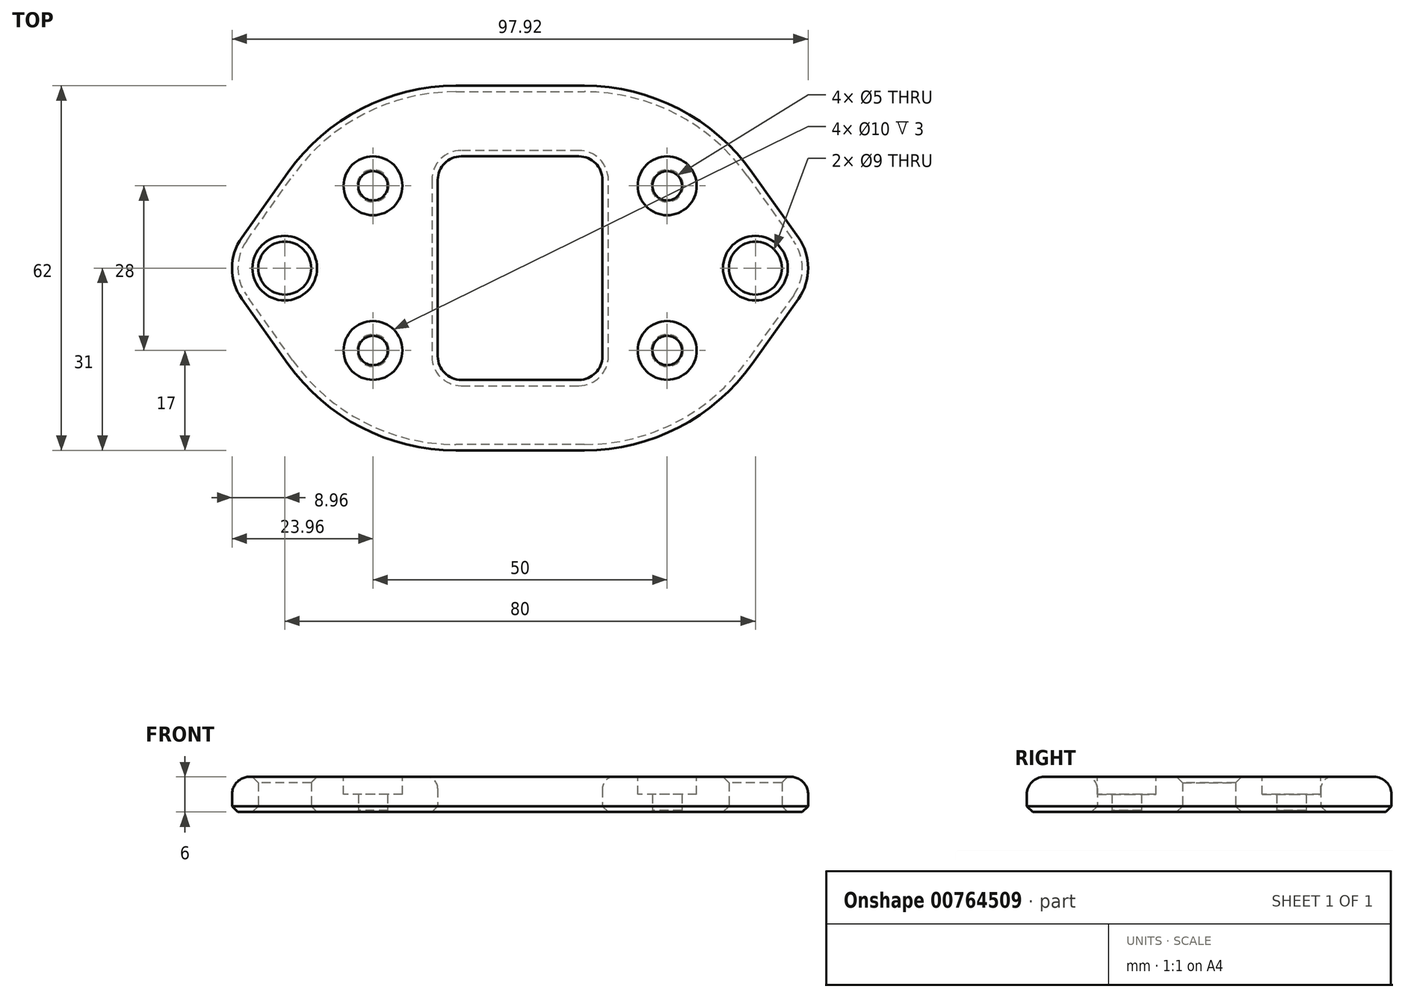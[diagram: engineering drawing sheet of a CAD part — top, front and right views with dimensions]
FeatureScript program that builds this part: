
annotation { "Feature Type Name" : "Feature", "Feature Type Description" : "" }
export const myFeature = defineFeature(function(context is Context, id is Id, definition is map)
    precondition{}
    {
        {
            var Q0;
            Q0=qCreatedBy(makeId("Top.planeOp"),FACE);
            var sketch = newSketch(context, id + "F0", { "sketchPlane" : qUnion([Q0])});
            skLineSegment(sketch, "E0", {"start": v(0, 24.52) * mm, "end": v(0, -20.17) * mm, "construction": true});
            skLineSegment(sketch, "E1", {"start": v(-29.41, 0) * mm, "end": v(36.17, 0) * mm, "construction": true});
            skCircle(sketch, "E2", {"center": v(-25, 14) * mm, "radius": 2.5 * mm});
            skCircle(sketch, "E3", {"center": v(-40, 0) * mm, "radius": 4.5 * mm});
            skLineSegment(sketch, "E4", {"start": v(0, 19) * mm, "end": v(-10, 19) * mm});
            skLineSegment(sketch, "E5", {"start": v(-14, 15) * mm, "end": v(-14, 10) * mm});
            skLineSegment(sketch, "E6", {"start": v(-20.5, 8) * mm, "end": v(-20.5, 8) * mm});
            skPoint(sketch, "E7.orphan", {"position": v(-14, 0) * mm});
            skPoint(sketch, "E8.visualSharp", {"position": v(-14, 19) * mm});
            skArc(sketch, "E8.filletArc", {"start": v(-10, 19) * mm, "mid": v(-12.83, 17.83) * mm, "end": v(-14, 15) * mm});
            skPoint(sketch, "E9.visualSharp", {"position": v(-14, 8) * mm});
            skPoint(sketch, "E10.visualSharp", {"position": v(-22.5, 8) * mm});
            skLineSegment(sketch, "E11.MirrorCS", {"start": v(-20.5, -8) * mm, "end": v(-20.5, -8) * mm});
            skLineSegment(sketch, "E12.MirrorCS", {"start": v(-14, -15) * mm, "end": v(-14, -10) * mm});
            skArc(sketch, "E13.MirrorCS", {"start": v(-10, -19) * mm, "mid": v(-12.83, -17.83) * mm, "end": v(-14, -15) * mm});
            skPoint(sketch, "E14.MirrorP", {"position": v(-14, -8) * mm});
            skPoint(sketch, "E15.MirrorP", {"position": v(-22.5, -8) * mm});
            skPoint(sketch, "E16.MirrorP", {"position": v(-14, -19) * mm});
            skCircle(sketch, "E17.MirrorC", {"center": v(-25, -14) * mm, "radius": 2.5 * mm});
            skLineSegment(sketch, "E18.MirrorCS", {"start": v(0, -19) * mm, "end": v(-10, -19) * mm});
            skLineSegment(sketch, "E19", {"start": v(0, -31) * mm, "end": v(-10.92, -31) * mm});
            skPoint(sketch, "E20", {"position": v(-51, 0) * mm});
            skLineSegment(sketch, "E21", {"start": v(-47.3, -5.2) * mm, "end": v(-39.46, -16.26) * mm});
            skLineSegment(sketch, "E22", {"start": v(0, 31) * mm, "end": v(-10.92, 31) * mm});
            skLineSegment(sketch, "E23", {"start": v(-39.46, 16.26) * mm, "end": v(-47.3, 5.2) * mm});
            skArc(sketch, "E24.filletArc", {"start": v(-47.3, 5.2) * mm, "mid": v(-48.96, 0) * mm, "end": v(-47.3, -5.2) * mm});
            skPoint(sketch, "E25.visualSharp", {"position": v(-29, -31) * mm});
            skArc(sketch, "E25.filletArc", {"start": v(-39.46, -16.26) * mm, "mid": v(-26.98, -27.1) * mm, "end": v(-10.92, -31) * mm});
            skPoint(sketch, "E26.visualSharp", {"position": v(-29, 31) * mm});
            skArc(sketch, "E26.filletArc", {"start": v(-10.92, 31) * mm, "mid": v(-26.98, 27.1) * mm, "end": v(-39.46, 16.26) * mm});
            skLineSegment(sketch, "E27.MirrorCS", {"start": v(20.5, -8) * mm, "end": v(20.5, -8) * mm});
            skLineSegment(sketch, "E28.MirrorCS", {"start": v(20.5, 8) * mm, "end": v(20.5, 8) * mm});
            skArc(sketch, "E29.MirrorCS", {"start": v(47.3, 5.2) * mm, "mid": v(48.96, 0) * mm, "end": v(47.3, -5.2) * mm});
            skLineSegment(sketch, "E30.MirrorCS", {"start": v(14, 15) * mm, "end": v(14, 10) * mm});
            skLineSegment(sketch, "E31.MirrorCS", {"start": v(14, -15) * mm, "end": v(14, -10) * mm});
            skPoint(sketch, "E32.MirrorP", {"position": v(51, 0) * mm});
            skArc(sketch, "E33.MirrorCS", {"start": v(10, -19) * mm, "mid": v(12.83, -17.83) * mm, "end": v(14, -15) * mm});
            skArc(sketch, "E34.MirrorCS", {"start": v(10, 19) * mm, "mid": v(12.83, 17.83) * mm, "end": v(14, 15) * mm});
            skArc(sketch, "E35.MirrorCS", {"start": v(39.46, -16.26) * mm, "mid": v(26.98, -27.1) * mm, "end": v(10.92, -31) * mm});
            skCircle(sketch, "E36.MirrorC", {"center": v(25, -14) * mm, "radius": 2.5 * mm});
            skPoint(sketch, "E37.MirrorP", {"position": v(22.5, -8) * mm});
            skLineSegment(sketch, "E38.MirrorCS", {"start": v(47.3, -5.2) * mm, "end": v(39.46, -16.26) * mm});
            skLineSegment(sketch, "E39.MirrorCS", {"start": v(39.46, 16.26) * mm, "end": v(47.3, 5.2) * mm});
            skArc(sketch, "E40.MirrorCS", {"start": v(10.92, 31) * mm, "mid": v(26.98, 27.1) * mm, "end": v(39.46, 16.26) * mm});
            skPoint(sketch, "E41.MirrorP", {"position": v(22.5, 8) * mm});
            skPoint(sketch, "E42.MirrorP", {"position": v(14, 19) * mm});
            skPoint(sketch, "E43.MirrorP", {"position": v(29, -31) * mm});
            skPoint(sketch, "E44.MirrorP", {"position": v(14, 0) * mm});
            skPoint(sketch, "E45.MirrorP", {"position": v(29, 31) * mm});
            skCircle(sketch, "E46.MirrorC", {"center": v(40, 0) * mm, "radius": 4.5 * mm});
            skPoint(sketch, "E47.MirrorP", {"position": v(14, -8) * mm});
            skCircle(sketch, "E48.MirrorC", {"center": v(25, 14) * mm, "radius": 2.5 * mm});
            skPoint(sketch, "E49.MirrorP", {"position": v(14, 8) * mm});
            skPoint(sketch, "E50.MirrorP", {"position": v(14, -19) * mm});
            skLineSegment(sketch, "E51.MirrorCS", {"start": v(0, 31) * mm, "end": v(10.92, 31) * mm});
            skLineSegment(sketch, "E52.MirrorCS", {"start": v(0, 19) * mm, "end": v(10, 19) * mm});
            skLineSegment(sketch, "E53.MirrorCS", {"start": v(0, -19) * mm, "end": v(10, -19) * mm});
            skLineSegment(sketch, "E54.MirrorCS", {"start": v(0, -31) * mm, "end": v(10.92, -31) * mm});
            skLineSegment(sketch, "E55", {"start": v(-14, 10) * mm, "end": v(-14, -10) * mm});
            skLineSegment(sketch, "E56", {"start": v(14, 10) * mm, "end": v(14, -10) * mm});
            skPoint(sketch, "E57.MirrorCS.end.orphan", {"position": v(22.5, 0) * mm});
            skPoint(sketch, "E57.MirrorCS.start.orphan", {"position": v(22.5, 6) * mm});
            skPoint(sketch, "E58.MirrorCS.start.orphan", {"position": v(22.5, -6) * mm});
            skPoint(sketch, "E59.end.orphan", {"position": v(-22.5, 0) * mm});
            skPoint(sketch, "E59.start.orphan", {"position": v(-22.5, 6) * mm});
            skPoint(sketch, "E60.MirrorCS.start.orphan", {"position": v(-22.5, -6) * mm});
            skSolve(sketch);
        }
        {
            var Q0;
            Q0=qSketchRegion(id+"F0",true);
            extrude(context, id + "F1", {"entities" : qUnion([Q0]), "depth" : 6 * mm, "offsetDistance" : 25 * mm});
        }
        {
            var Q0;
            {var subQ0=sQuery(id+"F0.wireOp",EDGE,"E40.MirrorCS");var subQ1=sQuery(id+"F0.wireOp",EDGE,"E39.MirrorCS");var subQ2=sQuery(id+"F0.wireOp",EDGE,"E57.MirrorCS");var subQ3=sQuery(id+"F0.wireOp",EDGE,"E58.MirrorCS");var subQ4=sQuery(id+"F0.wireOp",EDGE,"E34.MirrorCS");var subQ5=sQuery(id+"F0.wireOp",EDGE,"E26.filletArc");var subQ6=sQuery(id+"F0.wireOp",EDGE,"E24.filletArc");var subQ7=sQuery(id+"F0.wireOp",EDGE,"E23");var subQ8=sQuery(id+"F0.wireOp",EDGE,"E29.MirrorCS");var subQ9=sQuery(id+"F0.wireOp",EDGE,"E52.MirrorCS");var subQ10=sQuery(id+"F0.wireOp",EDGE,"E4");var subQ11=sQuery(id+"F0.wireOp",EDGE,"E28.MirrorCS");var subQ12=sQuery(id+"F0.wireOp",EDGE,"E3");var subQ13=sQuery(id+"F0.wireOp",EDGE,"E5");var subQ14=sQuery(id+"F0.wireOp",EDGE,"E2");var subQ15=sQuery(id+"F0.wireOp",EDGE,"E6");var subQ16=sQuery(id+"F0.wireOp",EDGE,"a55919db-5f6a-430a-85d6-64e5501b8bc05.MirrorCS");var subQ17=sQuery(id+"F0.wireOp",EDGE,"E60.MirrorCS");var subQ18=sQuery(id+"F0.wireOp",EDGE,"E59");var subQ19=sQuery(id+"F0.wireOp",EDGE,"E30.MirrorCS");var subQ20=sQuery(id+"F0.wireOp",EDGE,"E8.filletArc");var subQ21=sQuery(id+"F0.wireOp",EDGE,"a55919db-5f6a-430a-85d6-64e5501b8bc07.MirrorCS");var subQ22=sQuery(id+"F0.wireOp",EDGE,"E9.filletArc");var subQ23=sQuery(id+"F0.wireOp",EDGE,"E51.MirrorCS");var subQ24=sQuery(id+"F0.wireOp",EDGE,"E22");var subQ25=sQuery(id+"F0.wireOp",EDGE,"E10.filletArc");var subQ26=sQuery(id+"F0.wireOp",EDGE,"E46.MirrorC");var subQ27=sQuery(id+"F0.wireOp",EDGE,"E48.MirrorC");Q0=makeQuery(id+"F5VNmm26oAdcOlD_1.boolean.opBoolean","SPLIT",FACE,{"disambiguationData":[TD([makeQuery(id+"F1.opExtrude","SWEPT_FACE",FACE,{"disambiguationData":[OSD([subQ14])]})])],"derivedFrom":makeQuery(id+"F1.opExtrude","CAP_FACE",FACE,{"disambiguationData":[OSD([subQ14,subQ12,subQ10,subQ13,subQ15,subQ18,subQ20,subQ22,subQ25,sQuery(id+"F0.wireOp",EDGE,"27876a6a-8a0b-4b51-943c-244007aa9b000.MirrorCS"),sQuery(id+"F0.wireOp",EDGE,"27876a6a-8a0b-4b51-943c-244007aa9b001.MirrorCS"),sQuery(id+"F0.wireOp",EDGE,"E11.MirrorCS"),sQuery(id+"F0.wireOp",EDGE,"E12.MirrorCS"),sQuery(id+"F0.wireOp",EDGE,"E13.MirrorCS"),sQuery(id+"F0.wireOp",EDGE,"E17.MirrorC"),sQuery(id+"F0.wireOp",EDGE,"E18.MirrorCS"),subQ17,sQuery(id+"F0.wireOp",EDGE,"E19"),sQuery(id+"F0.wireOp",EDGE,"E21"),subQ24,subQ7,subQ6,sQuery(id+"F0.wireOp",EDGE,"E25.filletArc"),subQ5,sQuery(id+"F0.wireOp",EDGE,"E27.MirrorCS"),subQ11,subQ8,sQuery(id+"F0.wireOp",EDGE,"a55919db-5f6a-430a-85d6-64e5501b8bc03.MirrorCS"),sQuery(id+"F0.wireOp",EDGE,"a55919db-5f6a-430a-85d6-64e5501b8bc04.MirrorCS"),subQ16,subQ19,subQ21,sQuery(id+"F0.wireOp",EDGE,"E31.MirrorCS"),sQuery(id+"F0.wireOp",EDGE,"E33.MirrorCS"),subQ4,sQuery(id+"F0.wireOp",EDGE,"E35.MirrorCS"),sQuery(id+"F0.wireOp",EDGE,"E36.MirrorC"),subQ3,sQuery(id+"F0.wireOp",EDGE,"E38.MirrorCS"),subQ1,subQ0,subQ26,subQ27,subQ2,subQ23,subQ9,sQuery(id+"F0.wireOp",EDGE,"E53.MirrorCS"),sQuery(id+"F0.wireOp",EDGE,"E54.MirrorCS")])],"isStart":false})});}
            var sketch = newSketch(context, id + "F2", { "sketchPlane" : qUnion([Q0])});
            skCircle(sketch, "E61", {"center": v(-25, 14) * mm, "radius": 5 * mm});
            skCircle(sketch, "E62", {"center": v(25, 14) * mm, "radius": 5 * mm});
            skCircle(sketch, "E63", {"center": v(25, -14) * mm, "radius": 5 * mm});
            skCircle(sketch, "E64", {"center": v(-25, -14) * mm, "radius": 5 * mm});
            skSolve(sketch);
        }
        {
            var Q0;
            Q0=qSketchRegion(id+"F2",true);
            extrude(context, id + "F3", {"entities" : qUnion([Q0]), "operationType" : NewBodyOperationType.REMOVE, "oppositeDirection" : true, "depth" : 3 * mm, "offsetDistance" : 25 * mm});
        }
        {
            var Q0;
            Q0=makeQuery(id+"F1.opExtrude","CAP_EDGE",EDGE,{"disambiguationData":[OSD([sQuery(id+"F0.wireOp",EDGE,"E22"),sQuery(id+"F0.wireOp",EDGE,"E51.MirrorCS")])],"isStart":false});
            fillet(context, id + "F4", {"entities" : qUnion([Q0]), "radius" : 3 * mm, "tangentPropagation" : true, "allowEdgeOverflow" : false});
        }
        {
            var Q0;
            Q0=makeQuery(id+"F1.opExtrude","CAP_EDGE",EDGE,{"disambiguationData":[OSD([sQuery(id+"F0.wireOp",EDGE,"E35.MirrorCS")])],"isStart":true});
            chamfer(context, id + "F5", {"entities" : qUnion([Q0]), "width" : 1 * mm, "tangentPropagation" : true});
        }
        {
            var Q0;
            Q0=makeQuery(id+"F1.opExtrude","CAP_EDGE",EDGE,{"disambiguationData":[OSD([sQuery(id+"F0.wireOp",EDGE,"E5"),sQuery(id+"F0.wireOp",EDGE,"E12.MirrorCS"),sQuery(id+"F0.wireOp",EDGE,"E55")])],"isStart":true});
            chamfer(context, id + "F6", {"entities" : qUnion([Q0]), "width" : 1 * mm, "tangentPropagation" : true});
        }
        {
            var Q0;
            Q0=makeQuery(id+"F1.opExtrude","CAP_EDGE",EDGE,{"disambiguationData":[OSD([sQuery(id+"F0.wireOp",EDGE,"E3")])],"isStart":false});
            var Q1;
            Q1=makeQuery(id+"F1.opExtrude","CAP_EDGE",EDGE,{"disambiguationData":[OSD([sQuery(id+"F0.wireOp",EDGE,"E46.MirrorC")])],"isStart":false});
            var Q2;
            Q2=makeQuery(id+"F1.opExtrude","CAP_EDGE",EDGE,{"disambiguationData":[OSD([sQuery(id+"F0.wireOp",EDGE,"E46.MirrorC")])],"isStart":true});
            var Q3;
            Q3=makeQuery(id+"F1.opExtrude","CAP_EDGE",EDGE,{"disambiguationData":[OSD([sQuery(id+"F0.wireOp",EDGE,"E3")])],"isStart":true});
            chamfer(context, id + "F7", {"entities" : qUnion([Q0, Q1, Q2, Q3]), "width" : 1 * mm, "tangentPropagation" : true});
        }
        {
            var Q0;
            Q0=makeQuery(id+"F3.boolean.opBoolean","COPY",EDGE,{"derivedFrom":makeQuery(id+"F3.opExtrude","CAP_EDGE",EDGE,{"disambiguationData":[OSD([sQuery(id+"F2.wireOp",EDGE,"E64")])],"isStart":true})});
            var Q1;
            Q1=makeQuery(id+"F3.boolean.opBoolean","COPY",EDGE,{"derivedFrom":makeQuery(id+"F3.opExtrude","CAP_EDGE",EDGE,{"disambiguationData":[OSD([sQuery(id+"F2.wireOp",EDGE,"E61")])],"isStart":true})});
            var Q2;
            Q2=makeQuery(id+"F3.boolean.opBoolean","COPY",EDGE,{"derivedFrom":makeQuery(id+"F3.opExtrude","CAP_EDGE",EDGE,{"disambiguationData":[OSD([sQuery(id+"F2.wireOp",EDGE,"E62")])],"isStart":true})});
            var Q3;
            Q3=makeQuery(id+"F3.boolean.opBoolean","COPY",EDGE,{"derivedFrom":makeQuery(id+"F3.opExtrude","CAP_EDGE",EDGE,{"disambiguationData":[OSD([sQuery(id+"F2.wireOp",EDGE,"E63")])],"isStart":true})});
            var Q4;
            Q4=makeQuery(id+"F1.opExtrude","CAP_EDGE",EDGE,{"disambiguationData":[OSD([sQuery(id+"F0.wireOp",EDGE,"E36.MirrorC")])],"isStart":true});
            var Q5;
            Q5=makeQuery(id+"F1.opExtrude","CAP_EDGE",EDGE,{"disambiguationData":[OSD([sQuery(id+"F0.wireOp",EDGE,"E48.MirrorC")])],"isStart":true});
            var Q6;
            Q6=makeQuery(id+"F1.opExtrude","CAP_EDGE",EDGE,{"disambiguationData":[OSD([sQuery(id+"F0.wireOp",EDGE,"E2")])],"isStart":true});
            var Q7;
            Q7=makeQuery(id+"F1.opExtrude","CAP_EDGE",EDGE,{"disambiguationData":[OSD([sQuery(id+"F0.wireOp",EDGE,"E17.MirrorC")])],"isStart":true});
            chamfer(context, id + "F8", {"entities" : qUnion([Q0, Q1, Q2, Q3, Q4, Q5, Q6, Q7]), "width" : 0.25 * mm, "tangentPropagation" : true});
        }
        {
            var Q0;
            Q0=makeQuery(id+"F1.opExtrude","CAP_EDGE",EDGE,{"disambiguationData":[OSD([sQuery(id+"F0.wireOp",EDGE,"E4"),sQuery(id+"F0.wireOp",EDGE,"E52.MirrorCS")])],"isStart":false});
            fillet(context, id + "F9", {"entities" : qUnion([Q0]), "radius" : 2 * mm, "tangentPropagation" : true, "allowEdgeOverflow" : false});
        }
    });
